# Revit family: ORION LED
name_source: partatom
category: Осветительные приборы
revit_build: Autodesk Revit 2016 (Build: 20161004_0715(x64)
units: mm (PartAtom-declared; Revit-internal decimal feet)

## family parameters
Источник света = Нет
Общий = Нет
Основа = Грань
При загрузке вырезать с полостями = Нет
Размер круглого соединителя = Использовать диаметр
Тип детали = Нормальный
Точка расчета площади = Нет

## types (2) — shared parameters
ADSK_Единица измерения = Шт.
ADSK_Завод-изготовитель = ООО МГК Световые технологии
ADSK_Классификация нагрузок = Прочее
ADSK_Количество фаз = 1
ADSK_Количество фаз числовое = 1
ADSK_Коэффициент мощности = 0.97
ADSK_Наименование = Светильники серии ORION предназначены для освещения взрывоопасных зон всех классов помещений и наружных установок предприятий нефтегазовой и нефтехимической отрасли согласно маркировке взрывозащиты
ADSK_Напряжение = 230 В
ADSK_Номинальная мощность = 0 кВт
ADSK_Полная мощность = 0 кВ·А
ADSK_Размер_Ширина = 180 мм
ADSK_Ток = 0 А
IP Class = IP66
URL = https://ltcompany.com
Блок аварийного питания = Нет
Группа модели = Светильники
Да = Нет
Изготовитель = ООО МГК Световые технологии
Класс Защиты = I
Класс пожароопасности = П-I,II,IIa,ІІІ
Климатическая зона = УХЛ1
Код по классификатору = D5020200
Корпус = Cерый металл матовый
Нет = Нет
Область использования = Нефтегазовая промышленность
Описание = Светильники серии ORION предназначены для освещения взрывоопасных зон всех классов помещений и наружных установок предприятий нефтегазовой и нефтехимической отрасли согласно маркировке взрывозащиты
Плафон = Плафон прозрачный
Полная установленная мощность = 0 кВ·А
Тип ИС = LED
Тип ПРА = Драйвер
Тип продукции = Светильник
zero-valued in all types: Отметка по умолчанию

## per-type parameters (varying)
| type | ADSK_Код изделия | ADSK_Масса | ADSK_Размер_Высота | ADSK_Энергоэффективность | L | Выбор ИС | Крепление | Крепление.скоба | Крепление.труба |
| ORION LED 20G Ex | 1585000100 | 3.6 | 286 мм | 100 лм/Вт | 0 мм | IES_ORION LED : ORION LED 20G Ex | 3 мм | Нет | Да |
| ORION LED 30B Ex | 1585000110 | 3.7 | 498 мм | 98 лм/Вт | 200 мм | IES_ORION LED : ORION LED 30B Ex | 0 мм | Да | Нет |
